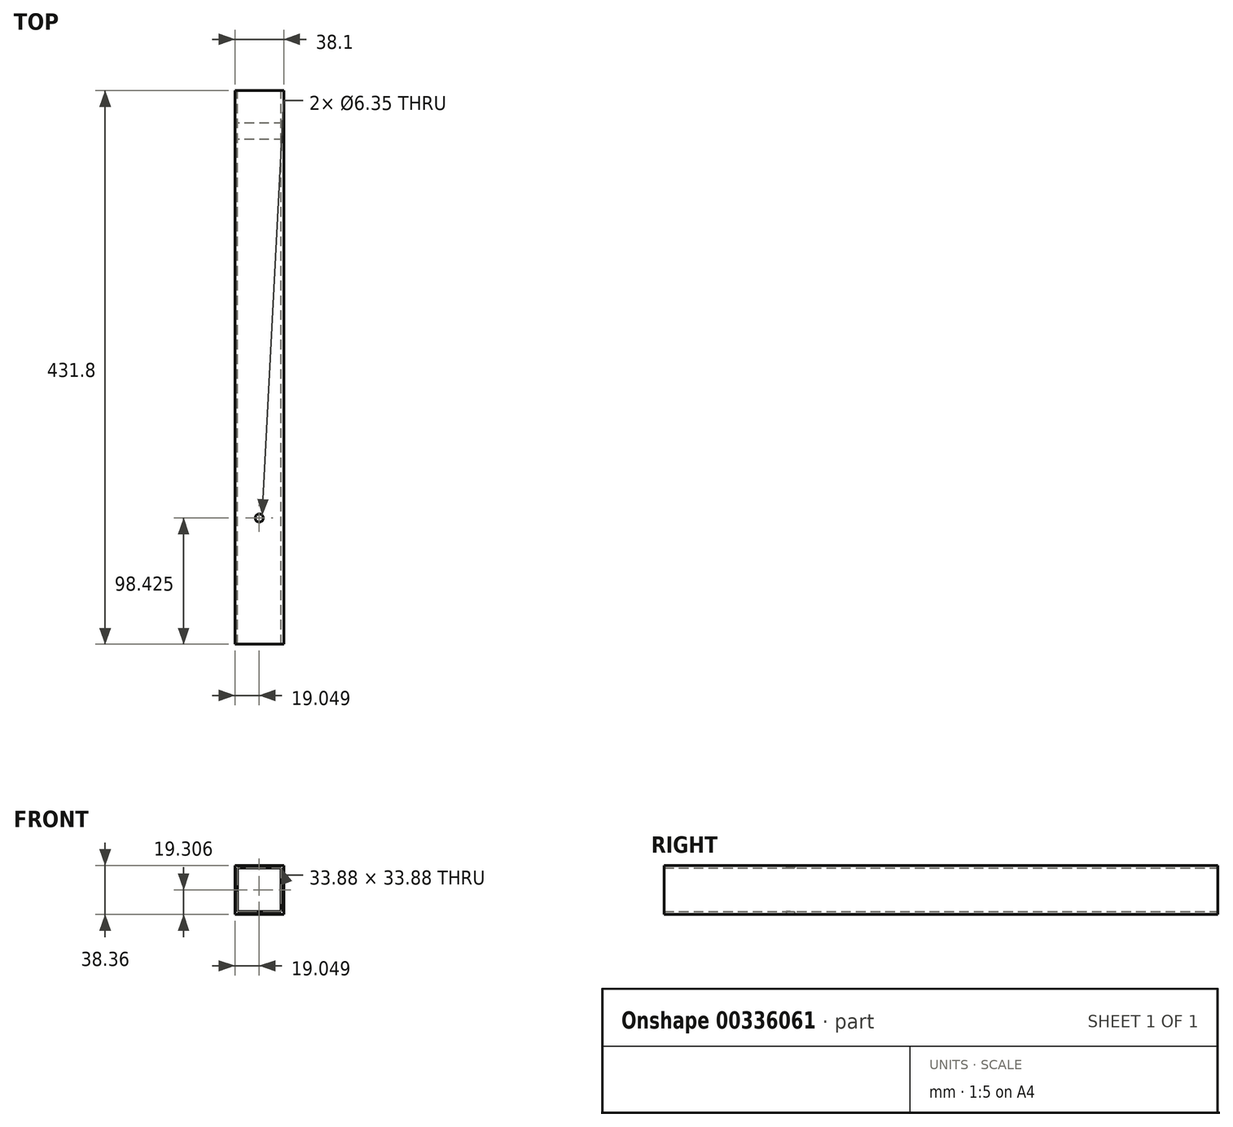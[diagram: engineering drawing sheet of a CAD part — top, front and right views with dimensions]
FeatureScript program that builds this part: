
annotation { "Feature Type Name" : "Feature", "Feature Type Description" : "" }
export const myFeature = defineFeature(function(context is Context, id is Id, definition is map)
    precondition{}
    {
        {
            var Q0;
            Q0=qCreatedBy(makeId("Front.planeOp"),FACE);
            var sketch = newSketch(context, id + "F0", { "sketchPlane" : qUnion([Q0])});
            skLineSegment(sketch, "E0.bottom", {"start": v(-64.17, 38.35) * mm, "end": v(-26.07, 38.35) * mm});
            skLineSegment(sketch, "E0.top", {"start": v(-64.17, 0.25) * mm, "end": v(-26.07, 0.25) * mm});
            skLineSegment(sketch, "E0.left", {"start": v(-64.17, 38.35) * mm, "end": v(-64.17, 0.25) * mm});
            skLineSegment(sketch, "E0.right", {"start": v(-26.07, 38.35) * mm, "end": v(-26.07, 0.25) * mm});
            skLineSegment(sketch, "E1.0", {"start": v(-28.18, 36.24) * mm, "end": v(-28.18, 2.35) * mm});
            skLineSegment(sketch, "E1.1", {"start": v(-62.06, 36.24) * mm, "end": v(-28.18, 36.24) * mm});
            skLineSegment(sketch, "E1.2", {"start": v(-62.06, 36.24) * mm, "end": v(-62.06, 2.35) * mm});
            skLineSegment(sketch, "E1.3", {"start": v(-62.06, 2.35) * mm, "end": v(-28.18, 2.35) * mm});
            skSolve(sketch);
        }
        {
            var Q0;
            Q0=makeQuery(id+"F0.imprint","IMPRINT",FACE,{"disambiguationData":[TD([[makeQuery(id+"F0.imprint","IMPRINT",EDGE,{"derivedFrom":sQuery(id+"F0.wireOp",EDGE,"E0.bottom")}),-1.0]])]});
            extrude(context, id + "F1", {"entities" : qUnion([Q0]), "depth" : 431.8 * mm});
        }
        {
            var Q0;
            Q0=makeQuery(id+"F1.opExtrude","SWEPT_FACE",FACE,{"disambiguationData":[OSD([sQuery(id+"F0.wireOp",EDGE,"E0.top")])]});
            var sketch = newSketch(context, id + "F2", { "sketchPlane" : qUnion([Q0])});
            skLineSegment(sketch, "E2", {"start": v(-26.07, 38.1) * mm, "end": v(-64.17, 38.1) * mm});
            skLineSegment(sketch, "E3", {"start": v(-26.07, 38.1) * mm, "end": v(-26.07, 25.4) * mm});
            skLineSegment(sketch, "E4", {"start": v(-26.07, 25.4) * mm, "end": v(-64.17, 25.4) * mm});
            skLineSegment(sketch, "E5", {"start": v(-64.17, 25.4) * mm, "end": v(-64.17, 38.1) * mm});
            skSolve(sketch);
        }
        {
            var Q0;
            Q0 = qSketchRegion(id + "F2", true);
            extrude(context, id + "F3", {"entities" : qUnion([Q0]), "operationType" : NewBodyOperationType.ADD, "depth" : 0.25 * mm});
        }
        {
            var Q0;
            {var subQ2=sQuery(id+"F0.wireOp",EDGE,"E0.top");Q0=makeQuery(id+"F3.boolean.opBoolean","SPLIT",FACE,{"disambiguationData":[TD([makeQuery(id+"F3.opExtrude","SWEPT_FACE",FACE,{"disambiguationData":[OSD([sQuery(id+"F2.wireOp",EDGE,"E2")])]})])],"derivedFrom":makeQuery(id+"F1.opExtrude","SWEPT_FACE",FACE,{"disambiguationData":[OSD([subQ2])]})});}
            var sketch = newSketch(context, id + "F4", { "sketchPlane" : qUnion([Q0])});
            skCircle(sketch, "E6", {"center": v(-45.12, 333.38) * mm, "radius": 3.18 * mm});
            skPoint(sketch, "E6.centerSnap0", {"position": v(-45.12, 431.8) * mm});
            skSolve(sketch);
        }
        {
            var Q0;
            Q0 = qSketchRegion(id + "F4", true);
            extrude(context, id + "F5", {"entities" : qUnion([Q0]), "operationType" : NewBodyOperationType.REMOVE, "oppositeDirection" : true, "depth" : 76.2 * mm});
        }
    });
